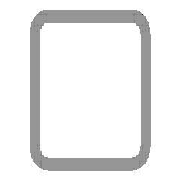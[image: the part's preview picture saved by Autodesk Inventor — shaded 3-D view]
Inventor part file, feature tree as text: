
AUTODESK INVENTOR PART (.ipt)
format: ipt  version: 2023.1 (Build 271208000, 208)  size: 130,560 bytes
history: native  units: mm (DEFAULTED — no unit token found)
features: other x4, sketch x3, plane x1
ambient origin geometry x8: Origin, YZ Plane, XZ Plane, XY Plane, X Axis, Y Axis, Z Axis, Center Point
bodies: Solid1 (feature_tree), Body (feature_tree)
feature tree (8):
  parser-record x1  (decoder bookkeeping rows leaked as tree rows — omitted from the tree; the rows remain in map.json)
  other  "Driven Length"
  other  "Start Plane"
  other  "End Plane"
  sketch  "Sketch"  dims[d10=50.8mm d11=50.8mm d12=3.175mm d13=25.4mm d14=482.6mm d15=25.4mm d16=25.4mm d17=6.35mm d18=90.0deg d19=457.2mm]
  sketch  "Sketch3"  dims[d3=457.2mm]
  plane  "Work Plane3"
  sketch  "Sketch4"  dims[d4=0.0mm]
